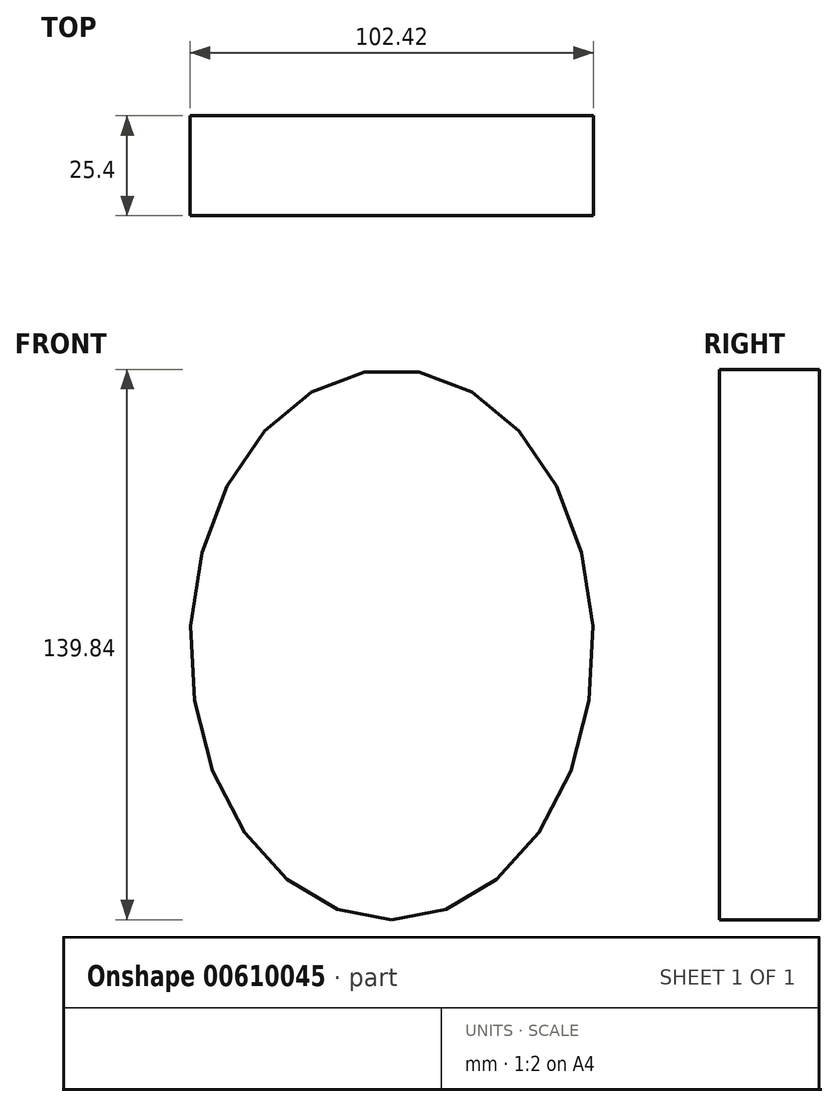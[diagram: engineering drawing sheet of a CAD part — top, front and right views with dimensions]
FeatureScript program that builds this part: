
annotation { "Feature Type Name" : "Feature", "Feature Type Description" : "" }
export const myFeature = defineFeature(function(context is Context, id is Id, definition is map)
    precondition{}
    {
        {
            var Q0;
            Q0=qCreatedBy(makeId("Front.planeOp"),FACE);
            var sketch = newSketch(context, id + "F0", { "sketchPlane" : qUnion([Q0])});
            skEllipse(sketch, "E0", {"center": v(0, 0) * mm, "majorRadius": 69.92 * mm, "minorRadius": 51.21 * mm, "majorAxis": v(0, -1)});
            skEllipse(sketch, "E1", {"center": v(0, 0) * mm, "majorRadius": 68.16 * mm, "minorRadius": 49.37 * mm, "majorAxis": v(0, -1)});
            skSolve(sketch);
        }
        {
            var Q0;
            Q0 = qSketchRegion(id + "F0", true);
            var Q1;
            Q1=makeQuery(id+"F0.imprint","IMPRINT",FACE,{"disambiguationData":[TD([[makeQuery(id+"F0.imprint","IMPRINT",EDGE,{"derivedFrom":sQuery(id+"F0.wireOp",EDGE,"E1")}),1.0]])]});
            extrude(context, id + "F1", {"entities" : qUnion([Q0, Q1]), "depth" : 25.4 * mm, "offsetDistance" : 25.4 * mm});
        }
    });
